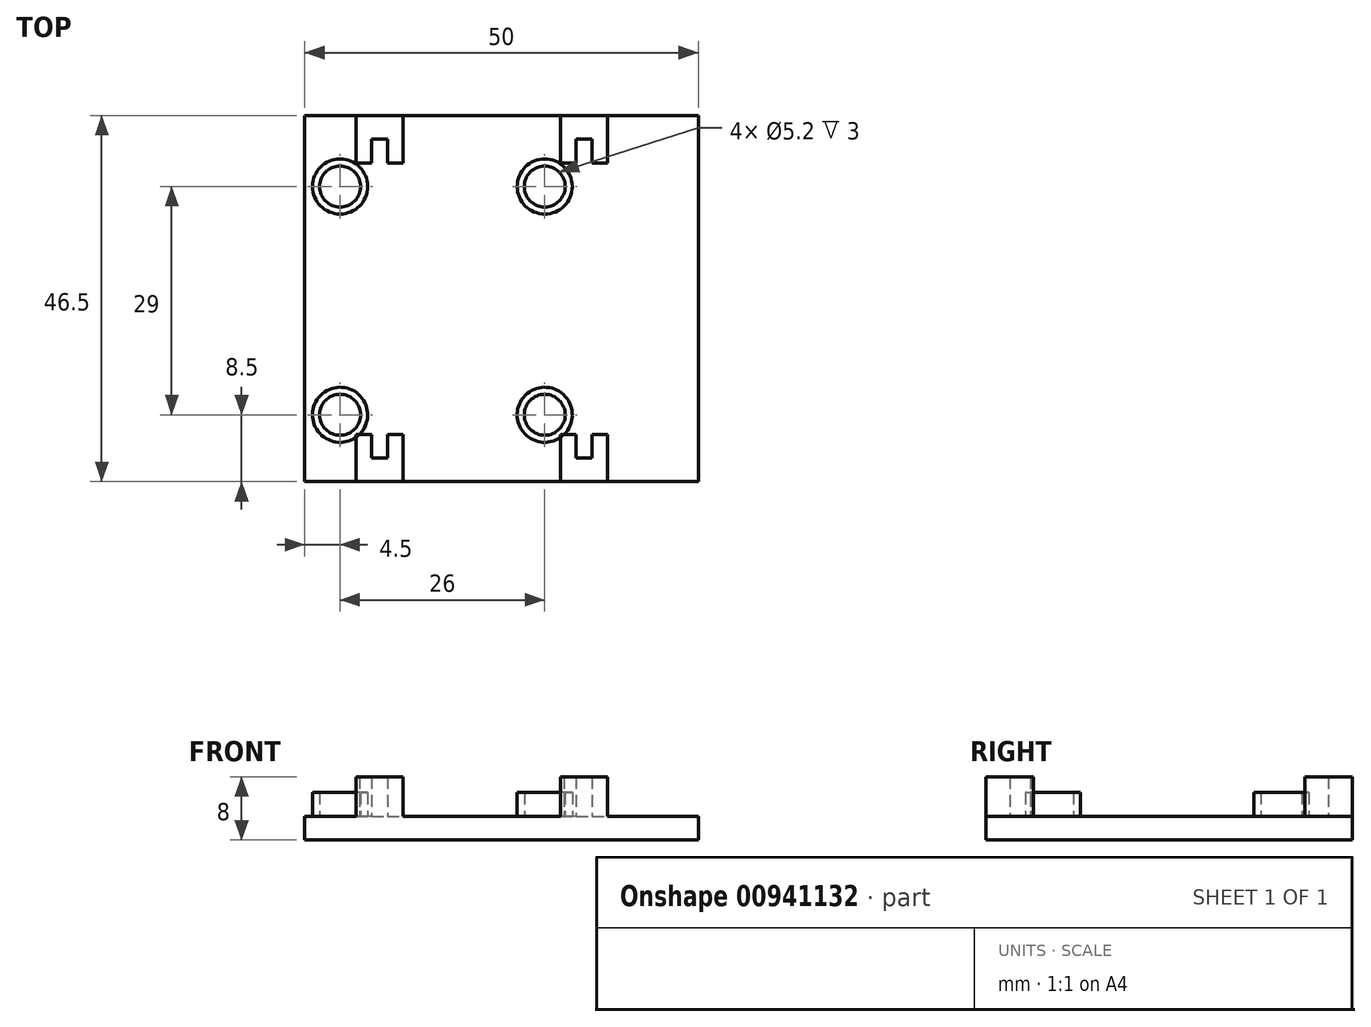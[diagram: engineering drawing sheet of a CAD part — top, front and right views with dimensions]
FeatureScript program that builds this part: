
annotation { "Feature Type Name" : "Feature", "Feature Type Description" : "" }
export const myFeature = defineFeature(function(context is Context, id is Id, definition is map)
    precondition{}
    {
        {
            var Q0;
            Q0=qCreatedBy(makeId("Top.planeOp"),FACE);
            var sketch = newSketch(context, id + "F0", { "sketchPlane" : qUnion([Q0])});
            skLineSegment(sketch, "E0.bottom", {"start": v(-25, 23.25) * mm, "end": v(25, 23.25) * mm});
            skLineSegment(sketch, "E0.top", {"start": v(-25, -23.25) * mm, "end": v(25, -23.25) * mm});
            skLineSegment(sketch, "E0.left", {"start": v(-25, 23.25) * mm, "end": v(-25, -23.25) * mm});
            skLineSegment(sketch, "E0.right", {"start": v(25, 23.25) * mm, "end": v(25, -23.25) * mm});
            skPoint(sketch, "E0.middle", {"position": v(0, 0) * mm});
            skSolve(sketch);
        }
        {
            var Q0;
            Q0 = qSketchRegion(id + "F0", true);
            extrude(context, id + "F1", {"entities" : qUnion([Q0]), "depth" : 3 * mm, "offsetDistance" : 25 * mm});
        }
        {
            var Q0;
            Q0=makeQuery(id+"F1.opExtrude","CAP_FACE",FACE,{"disambiguationData":[OSD([sQuery(id+"F0.wireOp",EDGE,"E0.bottom"),sQuery(id+"F0.wireOp",EDGE,"E0.top"),sQuery(id+"F0.wireOp",EDGE,"E0.left"),sQuery(id+"F0.wireOp",EDGE,"E0.right")])],"isStart":false});
            var sketch = newSketch(context, id + "F2", { "sketchPlane" : qUnion([Q0])});
            skCircle(sketch, "E1", {"center": v(-20.5, 14.25) * mm, "radius": 2.6 * mm});
            skCircle(sketch, "E2", {"center": v(-20.5, -14.75) * mm, "radius": 2.6 * mm});
            skCircle(sketch, "E3", {"center": v(5.5, 14.25) * mm, "radius": 2.6 * mm});
            skCircle(sketch, "E4", {"center": v(5.5, -14.75) * mm, "radius": 2.6 * mm});
            skLineSegment(sketch, "E5", {"start": v(-18.5, 23.25) * mm, "end": v(-18.5, 17.25) * mm});
            skLineSegment(sketch, "E6", {"start": v(-18.5, 17.25) * mm, "end": v(-16.5, 17.25) * mm});
            skLineSegment(sketch, "E7", {"start": v(-16.5, 17.25) * mm, "end": v(-16.5, 20.25) * mm});
            skLineSegment(sketch, "E8", {"start": v(-16.5, 20.25) * mm, "end": v(-14.5, 20.25) * mm});
            skLineSegment(sketch, "E9", {"start": v(-14.5, 20.25) * mm, "end": v(-14.5, 17.25) * mm});
            skLineSegment(sketch, "E10", {"start": v(-14.5, 17.25) * mm, "end": v(-12.5, 17.25) * mm});
            skLineSegment(sketch, "E11", {"start": v(-12.5, 17.25) * mm, "end": v(-12.5, 23.25) * mm});
            skLineSegment(sketch, "E12", {"start": v(7.5, 23.25) * mm, "end": v(7.5, 17.25) * mm});
            skLineSegment(sketch, "E13", {"start": v(7.5, 17.25) * mm, "end": v(9.5, 17.25) * mm});
            skLineSegment(sketch, "E14", {"start": v(9.5, 17.25) * mm, "end": v(9.5, 20.25) * mm});
            skLineSegment(sketch, "E15", {"start": v(9.5, 20.25) * mm, "end": v(11.5, 20.25) * mm});
            skLineSegment(sketch, "E16", {"start": v(11.5, 20.25) * mm, "end": v(11.5, 17.25) * mm});
            skLineSegment(sketch, "E17", {"start": v(11.5, 17.25) * mm, "end": v(13.5, 17.25) * mm});
            skLineSegment(sketch, "E18", {"start": v(13.5, 17.25) * mm, "end": v(13.5, 23.25) * mm});
            skLineSegment(sketch, "E19.top", {"start": v(-16.5, -20.25) * mm, "end": v(-14.5, -20.25) * mm});
            skLineSegment(sketch, "E19.left", {"start": v(-16.5, 20.25) * mm, "end": v(-16.5, -20.25) * mm});
            skLineSegment(sketch, "E19.right", {"start": v(-14.5, 20.25) * mm, "end": v(-14.5, -20.25) * mm});
            skLineSegment(sketch, "E20", {"start": v(-12.5, -23.25) * mm, "end": v(-12.5, -17.25) * mm});
            skLineSegment(sketch, "E21", {"start": v(-12.5, -17.25) * mm, "end": v(-14.5, -17.25) * mm});
            skLineSegment(sketch, "E22", {"start": v(-14.5, -17.25) * mm, "end": v(-16.5, -17.25) * mm});
            skLineSegment(sketch, "E23", {"start": v(-16.5, -17.25) * mm, "end": v(-18.5, -17.25) * mm});
            skLineSegment(sketch, "E24", {"start": v(-18.5, -17.25) * mm, "end": v(-18.5, -23.25) * mm});
            skLineSegment(sketch, "E25.top", {"start": v(9.5, -20.25) * mm, "end": v(11.5, -20.25) * mm});
            skLineSegment(sketch, "E25.left", {"start": v(9.5, 20.25) * mm, "end": v(9.5, -20.25) * mm});
            skLineSegment(sketch, "E25.right", {"start": v(11.5, 20.25) * mm, "end": v(11.5, -20.25) * mm});
            skLineSegment(sketch, "E26", {"start": v(9.5, -17.25) * mm, "end": v(7.5, -17.25) * mm});
            skLineSegment(sketch, "E27", {"start": v(7.5, -17.25) * mm, "end": v(7.5, -23.25) * mm});
            skLineSegment(sketch, "E28", {"start": v(11.5, -17.25) * mm, "end": v(13.5, -17.25) * mm});
            skLineSegment(sketch, "E29", {"start": v(13.5, -17.25) * mm, "end": v(13.5, -23.25) * mm});
            skCircle(sketch, "E30", {"center": v(-20.5, 14.25) * mm, "radius": 3.5 * mm});
            skCircle(sketch, "E31", {"center": v(5.5, 14.25) * mm, "radius": 3.5 * mm});
            skCircle(sketch, "E32", {"center": v(5.5, -14.75) * mm, "radius": 3.5 * mm});
            skCircle(sketch, "E33", {"center": v(-20.5, -14.75) * mm, "radius": 3.5 * mm});
            skSolve(sketch);
        }
        {
            var Q0;
            {var subQ5=sQuery(id+"F2.wireOp",EDGE,"E5");Q0=makeQuery(id+"F2.imprint","IMPRINT",FACE,{"disambiguationData":[TD([[makeQuery(id+"F2.imprint","IMPRINT",EDGE,{"derivedFrom":subQ5}),1.0]])]});}
            var Q1;
            {var subQ2=sQuery(id+"F2.wireOp",EDGE,"E12");Q1=makeQuery(id+"F2.imprint","IMPRINT",FACE,{"disambiguationData":[TD([[makeQuery(id+"F2.imprint","IMPRINT",EDGE,{"derivedFrom":subQ2}),1.0]])]});}
            var Q2;
            {var subQ2=sQuery(id+"F2.wireOp",EDGE,"E25.top");Q2=makeQuery(id+"F2.imprint","IMPRINT",FACE,{"disambiguationData":[TD([[makeQuery(id+"F2.imprint","IMPRINT",EDGE,{"derivedFrom":subQ2}),-1.0]])]});}
            var Q3;
            {var subQ2=sQuery(id+"F2.wireOp",EDGE,"E19.top");Q3=makeQuery(id+"F2.imprint","IMPRINT",FACE,{"disambiguationData":[TD([[makeQuery(id+"F2.imprint","IMPRINT",EDGE,{"derivedFrom":subQ2}),-1.0]])]});}
            extrude(context, id + "F3", {"entities" : qUnion([Q0, Q1, Q2, Q3]), "operationType" : NewBodyOperationType.ADD, "depth" : 5 * mm, "offsetDistance" : 25 * mm});
        }
        {
            var Q0;
            Q0=makeQuery(id+"F2.imprint","IMPRINT",FACE,{"disambiguationData":[TD([[makeQuery(id+"F2.imprint","IMPRINT",EDGE,{"derivedFrom":sQuery(id+"F2.wireOp",EDGE,"E1")}),-1.0]])]});
            var Q1;
            Q1=makeQuery(id+"F2.imprint","IMPRINT",FACE,{"disambiguationData":[TD([[makeQuery(id+"F2.imprint","IMPRINT",EDGE,{"derivedFrom":sQuery(id+"F2.wireOp",EDGE,"E3")}),-1.0]])]});
            var Q2;
            Q2=makeQuery(id+"F2.imprint","IMPRINT",FACE,{"disambiguationData":[TD([[makeQuery(id+"F2.imprint","IMPRINT",EDGE,{"derivedFrom":sQuery(id+"F2.wireOp",EDGE,"E4")}),-1.0]])]});
            var Q3;
            Q3=makeQuery(id+"F2.imprint","IMPRINT",FACE,{"disambiguationData":[TD([[makeQuery(id+"F2.imprint","IMPRINT",EDGE,{"derivedFrom":sQuery(id+"F2.wireOp",EDGE,"E2")}),-1.0]])]});
            extrude(context, id + "F4", {"entities" : qUnion([Q0, Q1, Q2, Q3]), "depth" : 3 * mm, "offsetDistance" : 25 * mm});
        }
    });
